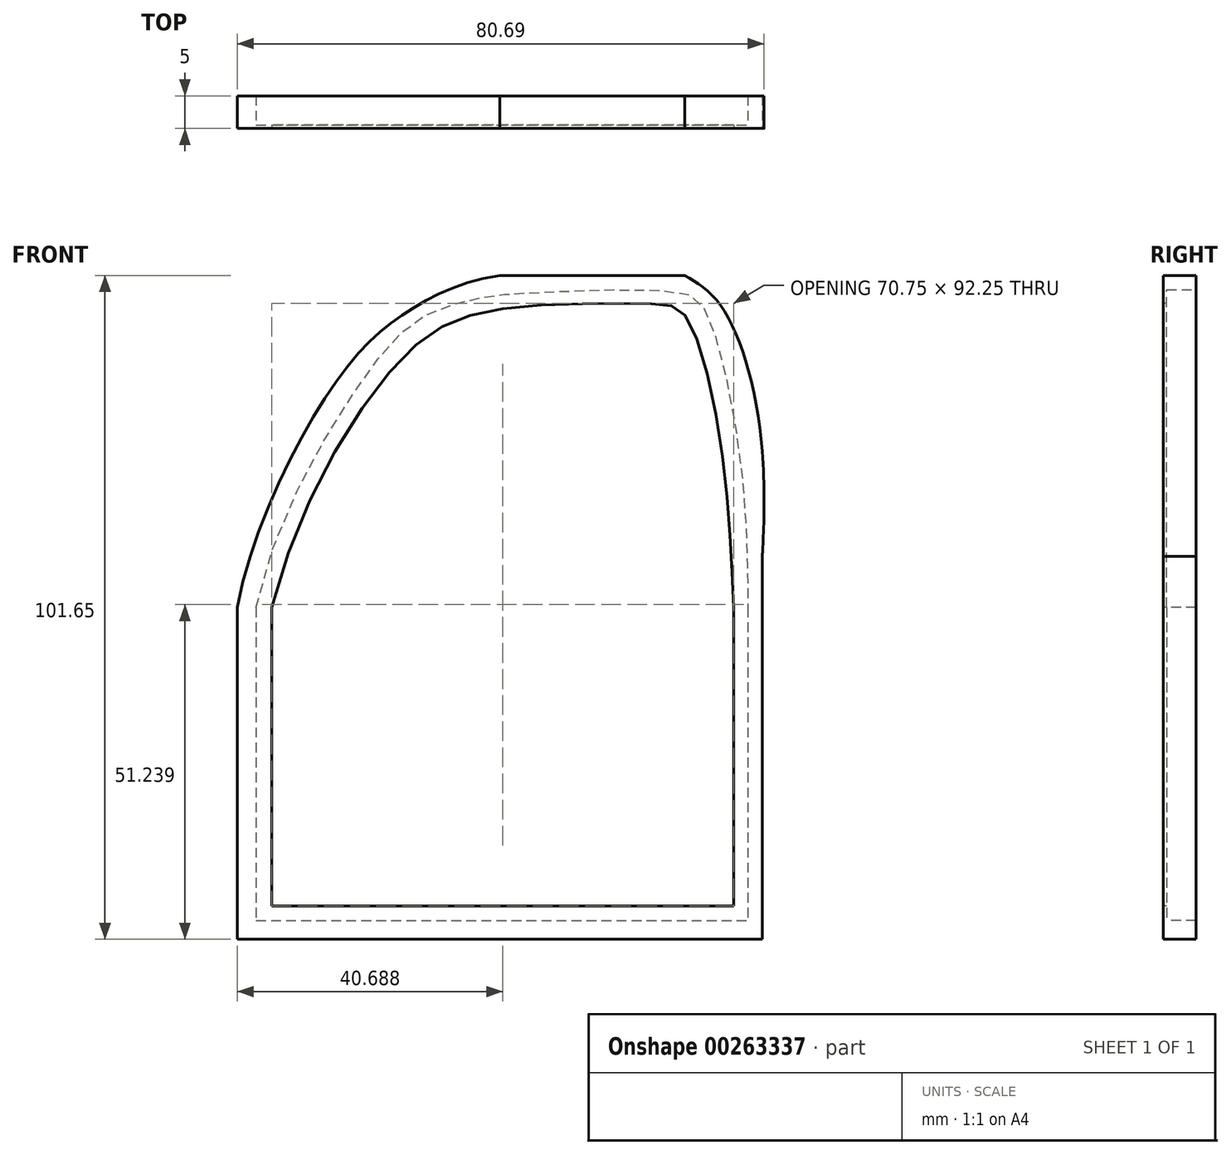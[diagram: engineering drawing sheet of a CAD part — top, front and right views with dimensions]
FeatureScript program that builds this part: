
annotation { "Feature Type Name" : "Feature", "Feature Type Description" : "" }
export const myFeature = defineFeature(function(context is Context, id is Id, definition is map)
    precondition{}
    {
        {
            var Q0;
            Q0=qCreatedBy(makeId("Front.planeOp"),FACE);
            var sketch = newSketch(context, id + "F0", { "sketchPlane" : qUnion([Q0])});
            skLineSegment(sketch, "E0.bottom", {"start": v(-6.38, 46.5) * mm, "end": v(21.95, 46.5) * mm});
            skLineSegment(sketch, "E0.top", {"start": v(-46.59, -55.14) * mm, "end": v(33.83, -55.14) * mm});
            skLineSegment(sketch, "E0.left", {"start": v(-46.59, -4.32) * mm, "end": v(-46.59, -55.14) * mm});
            skLineSegment(sketch, "E0.right", {"start": v(33.83, 19.6) * mm, "end": v(33.83, -55.14) * mm});
            skFitSpline(sketch, "E1", {"points": [v(-46.59, -4.32) * mm, v(-30.87, 31) * mm, v(-20.25, 41.13) * mm, v(-6.38, 46.5) * mm], "startDerivative": vector(17.33, 88.44) * mm, "endDerivative": vector(60.56, 8.43) * mm});
            skPoint(sketch, "E2.orphan", {"position": v(-46.59, 46.5) * mm});
            skFitSpline(sketch, "E3", {"points": [v(21.95, 46.5) * mm, v(27.63, 41.64) * mm, v(33.83, 19.6) * mm, v(33.83, 3.49) * mm, v(33.83, 3.37) * mm], "startDerivative": vector(25.35, -15.2) * mm, "endDerivative": vector(0.18, -3.1) * mm});
            skPoint(sketch, "E4.orphan", {"position": v(33.83, 46.5) * mm});
            skLineSegment(sketch, "E5.top", {"start": v(-43.68, -52.26) * mm, "end": v(31.62, -52.26) * mm});
            skLineSegment(sketch, "E5.left", {"start": v(-43.68, -4.32) * mm, "end": v(-43.68, -52.26) * mm});
            skLineSegment(sketch, "E5.right", {"start": v(31.62, -4.32) * mm, "end": v(31.62, -52.26) * mm});
            skFitSpline(sketch, "E6", {"points": [v(-43.68, -4.32) * mm, v(-27, 31) * mm, v(-17.27, 40.65) * mm, v(-7.5, 43.38) * mm, v(-1.6, 43.84) * mm, v(20.74, 44) * mm, v(25.12, 41.13) * mm, v(30.28, 19.6) * mm, v(31.62, -4.32) * mm], "startDerivative": vector(40.76, 206.76) * mm, "endDerivative": vector(0.55, -146.46) * mm});
            skLineSegment(sketch, "E7.top", {"start": v(-41.28, -50.03) * mm, "end": v(29.47, -50.03) * mm});
            skLineSegment(sketch, "E7.left", {"start": v(-41.28, -4.32) * mm, "end": v(-41.28, -50.03) * mm});
            skLineSegment(sketch, "E7.right", {"start": v(29.47, -4.32) * mm, "end": v(29.47, -50.03) * mm});
            skFitSpline(sketch, "E8", {"points": [v(29.47, -4.32) * mm, v(27.6, 19.6) * mm, v(21.96, 40.45) * mm, v(16.9, 42.14) * mm, v(-5.95, 41.4) * mm, v(-20.95, 34.2) * mm, v(-41.28, -4.32) * mm], "startDerivative": vector(-5.83, 122.07) * mm, "endDerivative": vector(-47.07, -192.85) * mm});
            skSolve(sketch);
        }
        {
            var Q0;
            Q0=qSketchRegion(id+"F0",true);
            extrude(context, id + "F1", {"entities" : qUnion([Q0]), "oppositeDirection" : true, "depth" : 5 * mm});
        }
        {
            var Q0;
            Q0=makeQuery(id+"F0.imprint","IMPRINT",FACE,{"disambiguationData":[TD([[makeQuery(id+"F0.imprint","IMPRINT",EDGE,{"derivedFrom":sQuery(id+"F0.wireOp",EDGE,"E5.top")}),1.0]])]});
            extrude(context, id + "F2", {"entities" : qUnion([Q0]), "operationType" : NewBodyOperationType.ADD, "oppositeDirection" : true, "depth" : 0.5 * mm});
        }
    });
